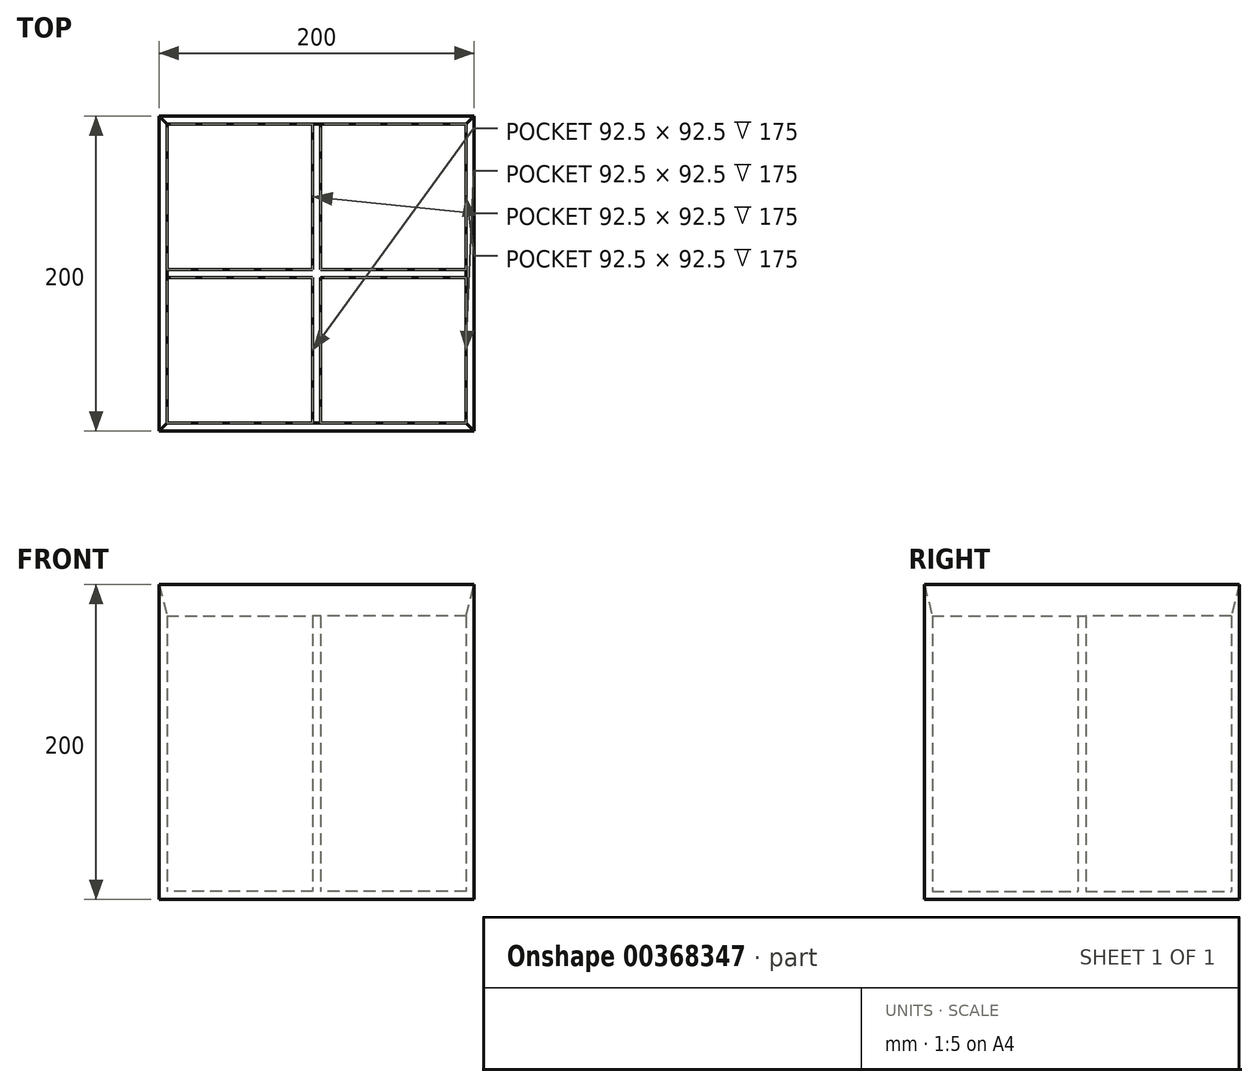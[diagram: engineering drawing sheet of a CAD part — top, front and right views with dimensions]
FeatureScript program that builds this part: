
annotation { "Feature Type Name" : "Feature", "Feature Type Description" : "" }
export const myFeature = defineFeature(function(context is Context, id is Id, definition is map)
    precondition{}
    {
        {
            var Q0;
            Q0=qCreatedBy(makeId("Top.planeOp"),FACE);
            var sketch = newSketch(context, id + "F0", { "sketchPlane" : qUnion([Q0])});
            skLineSegment(sketch, "E0.bottom", {"start": v(100, -100) * mm, "end": v(-100, -100) * mm});
            skLineSegment(sketch, "E0.top", {"start": v(100, 100) * mm, "end": v(-100, 100) * mm});
            skLineSegment(sketch, "E0.left", {"start": v(100, -100) * mm, "end": v(100, 100) * mm});
            skLineSegment(sketch, "E0.right", {"start": v(-100, -100) * mm, "end": v(-100, 100) * mm});
            skPoint(sketch, "E0.middle", {"position": v(0, 0) * mm});
            skLineSegment(sketch, "E1.0", {"start": v(95, 95) * mm, "end": v(-95, 95) * mm});
            skLineSegment(sketch, "E1.1", {"start": v(95, -95) * mm, "end": v(95, 95) * mm});
            skLineSegment(sketch, "E1.2", {"start": v(95, -95) * mm, "end": v(-95, -95) * mm});
            skLineSegment(sketch, "E1.3", {"start": v(-95, -95) * mm, "end": v(-95, 95) * mm});
            skLineSegment(sketch, "E2", {"start": v(-2.5, 95) * mm, "end": v(-2.5, -95) * mm});
            skLineSegment(sketch, "E3", {"start": v(2.5, 95) * mm, "end": v(2.5, -95) * mm});
            skLineSegment(sketch, "E4", {"start": v(-95, 2.5) * mm, "end": v(95, 2.5) * mm});
            skLineSegment(sketch, "E5", {"start": v(-95, -2.5) * mm, "end": v(95, -2.5) * mm});
            skSolve(sketch);
        }
        {
            var Q0;
            {var subQ0=sQuery(id+"F0.wireOp",EDGE,"E1.3");var subQ1=sQuery(id+"F0.wireOp",EDGE,"E1.0");var subQ2=makeQuery(id+"F0.imprint","INTERSECT",VERTEX,{"derivedFrom":[subQ1,subQ0]});Q0=makeQuery(id+"F0.imprint","IMPRINT",FACE,{"disambiguationData":[TD([[makeQuery(id+"F0.imprint","IMPRINT",EDGE,{"disambiguationData":[TD([[subQ2,1.0]])],"derivedFrom":subQ1}),1.0]])]});}
            var Q1;
            {var subQ0=sQuery(id+"F0.wireOp",EDGE,"E1.1");var subQ1=sQuery(id+"F0.wireOp",EDGE,"E1.0");var subQ2=makeQuery(id+"F0.imprint","INTERSECT",VERTEX,{"derivedFrom":[subQ1,subQ0]});Q1=makeQuery(id+"F0.imprint","IMPRINT",FACE,{"disambiguationData":[TD([[makeQuery(id+"F0.imprint","IMPRINT",EDGE,{"disambiguationData":[TD([[subQ2,-1.0]])],"derivedFrom":subQ1}),1.0]])]});}
            var Q2;
            {var subQ0=sQuery(id+"F0.wireOp",EDGE,"E1.2");var subQ1=sQuery(id+"F0.wireOp",EDGE,"E1.1");var subQ2=makeQuery(id+"F0.imprint","INTERSECT",VERTEX,{"derivedFrom":[subQ1,subQ0]});Q2=makeQuery(id+"F0.imprint","IMPRINT",FACE,{"disambiguationData":[TD([[makeQuery(id+"F0.imprint","IMPRINT",EDGE,{"disambiguationData":[TD([[subQ2,-1.0]])],"derivedFrom":subQ1}),1.0]])]});}
            var Q3;
            {var subQ0=sQuery(id+"F0.wireOp",EDGE,"E1.3");var subQ1=sQuery(id+"F0.wireOp",EDGE,"E1.2");var subQ2=makeQuery(id+"F0.imprint","INTERSECT",VERTEX,{"derivedFrom":[subQ1,subQ0]});Q3=makeQuery(id+"F0.imprint","IMPRINT",FACE,{"disambiguationData":[TD([[makeQuery(id+"F0.imprint","IMPRINT",EDGE,{"disambiguationData":[TD([[subQ2,1.0]])],"derivedFrom":subQ1}),-1.0]])]});}
            extrude(context, id + "F1", {"entities" : qUnion([Q0, Q1, Q2, Q3]), "depth" : 5 * mm});
        }
        {
            var Q0;
            {var subQ0=sQuery(id+"F0.wireOp",EDGE,"E4");var subQ1=sQuery(id+"F0.wireOp",EDGE,"E1.3");var subQ2=makeQuery(id+"F0.imprint","INTERSECT",VERTEX,{"derivedFrom":[subQ1,subQ0]});Q0=makeQuery(id+"F0.imprint","IMPRINT",FACE,{"disambiguationData":[TD([[makeQuery(id+"F0.imprint","IMPRINT",EDGE,{"disambiguationData":[TD([[subQ2,1.0]])],"derivedFrom":subQ1}),-1.0]])]});}
            var Q1;
            {var subQ0=sQuery(id+"F0.wireOp",EDGE,"E2");var subQ1=sQuery(id+"F0.wireOp",EDGE,"E1.2");var subQ2=makeQuery(id+"F0.imprint","INTERSECT",VERTEX,{"derivedFrom":[subQ1,subQ0]});Q1=makeQuery(id+"F0.imprint","IMPRINT",FACE,{"disambiguationData":[TD([[makeQuery(id+"F0.imprint","IMPRINT",EDGE,{"disambiguationData":[TD([[subQ2,1.0]])],"derivedFrom":subQ1}),-1.0]])]});}
            var Q2;
            {var subQ0=sQuery(id+"F0.wireOp",EDGE,"E4");var subQ1=sQuery(id+"F0.wireOp",EDGE,"E1.1");var subQ2=makeQuery(id+"F0.imprint","INTERSECT",VERTEX,{"derivedFrom":[subQ1,subQ0]});Q2=makeQuery(id+"F0.imprint","IMPRINT",FACE,{"disambiguationData":[TD([[makeQuery(id+"F0.imprint","IMPRINT",EDGE,{"disambiguationData":[TD([[subQ2,1.0]])],"derivedFrom":subQ1}),1.0]])]});}
            var Q3;
            {var subQ0=sQuery(id+"F0.wireOp",EDGE,"E2");var subQ1=sQuery(id+"F0.wireOp",EDGE,"E1.0");var subQ2=makeQuery(id+"F0.imprint","INTERSECT",VERTEX,{"derivedFrom":[subQ1,subQ0]});Q3=makeQuery(id+"F0.imprint","IMPRINT",FACE,{"disambiguationData":[TD([[makeQuery(id+"F0.imprint","IMPRINT",EDGE,{"disambiguationData":[TD([[subQ2,1.0]])],"derivedFrom":subQ1}),1.0]])]});}
            var Q4;
            {var subQ0=sQuery(id+"F0.wireOp",EDGE,"E4");var subQ1=sQuery(id+"F0.wireOp",EDGE,"E2");var subQ2=makeQuery(id+"F0.imprint","INTERSECT",VERTEX,{"derivedFrom":[subQ1,subQ0]});Q4=makeQuery(id+"F0.imprint","IMPRINT",FACE,{"disambiguationData":[TD([[makeQuery(id+"F0.imprint","IMPRINT",EDGE,{"disambiguationData":[TD([[subQ2,-1.0]])],"derivedFrom":subQ1}),1.0]])]});}
            extrude(context, id + "F2", {"entities" : qUnion([Q0, Q1, Q2, Q3, Q4]), "operationType" : NewBodyOperationType.ADD, "depth" : 180 * mm});
        }
        {
            var Q0;
            Q0=makeQuery(id+"F0.imprint","IMPRINT",FACE,{"disambiguationData":[TD([[makeQuery(id+"F0.imprint","IMPRINT",EDGE,{"derivedFrom":sQuery(id+"F0.wireOp",EDGE,"E0.bottom")}),-1.0]])]});
            extrude(context, id + "F3", {"entities" : qUnion([Q0]), "operationType" : NewBodyOperationType.ADD, "depth" : 200 * mm});
        }
        {
            var Q0;
            Q0=makeQuery(id+"F3.opExtrude","CAP_EDGE",EDGE,{"disambiguationData":[OSD([sQuery(id+"F0.wireOp",EDGE,"E1.3")])],"isStart":false});
            var Q1;
            Q1=makeQuery(id+"F3.opExtrude","CAP_EDGE",EDGE,{"disambiguationData":[OSD([sQuery(id+"F0.wireOp",EDGE,"E1.2")])],"isStart":false});
            var Q2;
            Q2=makeQuery(id+"F3.opExtrude","CAP_EDGE",EDGE,{"disambiguationData":[OSD([sQuery(id+"F0.wireOp",EDGE,"E1.1")])],"isStart":false});
            var Q3;
            Q3=makeQuery(id+"F3.opExtrude","CAP_EDGE",EDGE,{"disambiguationData":[OSD([sQuery(id+"F0.wireOp",EDGE,"E1.0")])],"isStart":false});
            chamfer(context, id + "F4", {"entities" : qUnion([Q0, Q1, Q2, Q3]), "chamferType" : ChamferType.TWO_OFFSETS, "width1" : 5 * mm, "oppositeDirection" : false, "width2" : 20 * mm, "tangentPropagation" : true});
        }
    });
